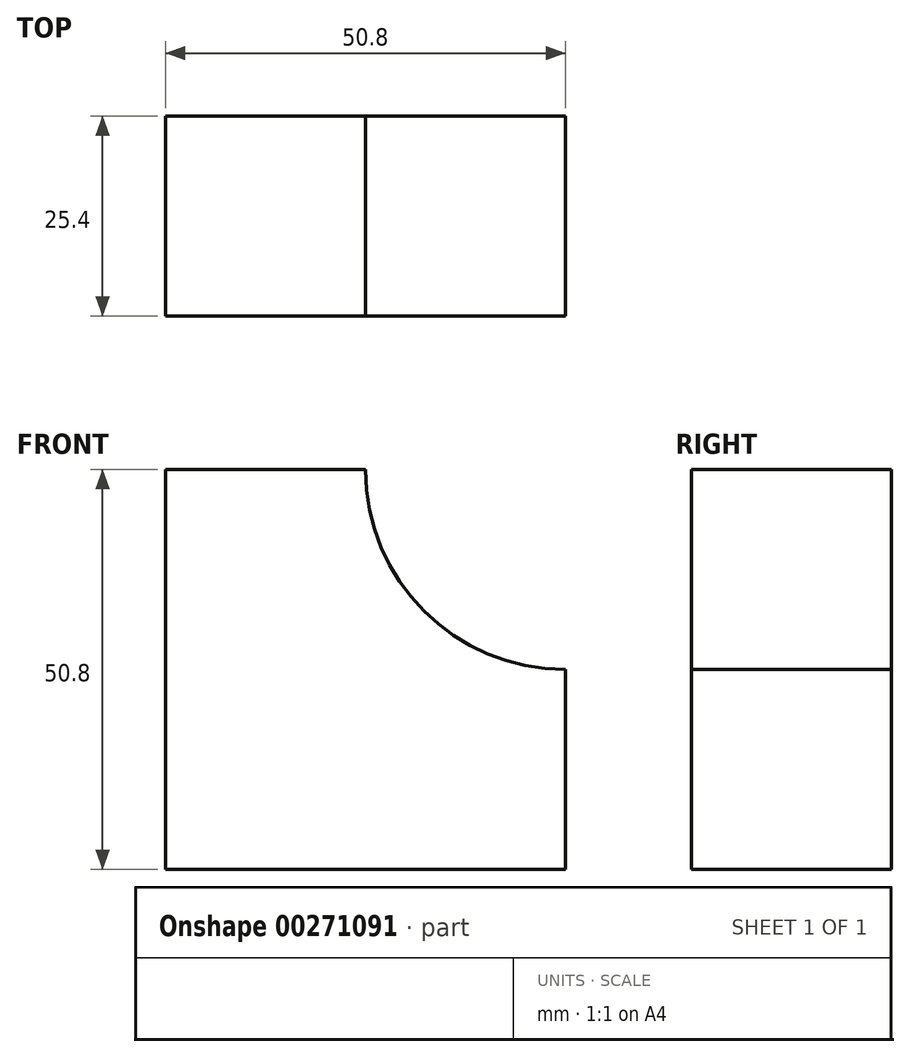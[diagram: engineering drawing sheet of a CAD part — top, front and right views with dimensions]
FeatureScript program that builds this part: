
annotation { "Feature Type Name" : "Feature", "Feature Type Description" : "" }
export const myFeature = defineFeature(function(context is Context, id is Id, definition is map)
    precondition{}
    {
        {
            var Q0;
            Q0=qCreatedBy(makeId("Front.planeOp"),FACE);
            var sketch = newSketch(context, id + "F0", { "sketchPlane" : qUnion([Q0])});
            skLineSegment(sketch, "E0", {"start": v(0, 50.8) * mm, "end": v(0, 0) * mm});
            skLineSegment(sketch, "E1", {"start": v(0, 0) * mm, "end": v(50.8, 0) * mm});
            skLineSegment(sketch, "E2", {"start": v(50.8, 0) * mm, "end": v(50.8, 25.4) * mm});
            skLineSegment(sketch, "E3", {"start": v(25.4, 50.8) * mm, "end": v(0, 50.8) * mm});
            skArc(sketch, "E4", {"start": v(25.4, 50.8) * mm, "mid": v(32.84, 32.84) * mm, "end": v(50.8, 25.4) * mm});
            skSolve(sketch);
        }
        {
            var Q0;
            Q0 = qSketchRegion(id + "F0", true);
            var Q1;
            Q1=makeQuery(id+"F0.imprint","IMPRINT",FACE,{"disambiguationData":[TD([[makeQuery(id+"F0.imprint","IMPRINT",EDGE,{"derivedFrom":sQuery(id+"F0.wireOp",EDGE,"E0")}),1.0]])]});
            extrude(context, id + "F1", {"entities" : qUnion([Q0, Q1]), "depth" : 25.4 * mm});
        }
    });
